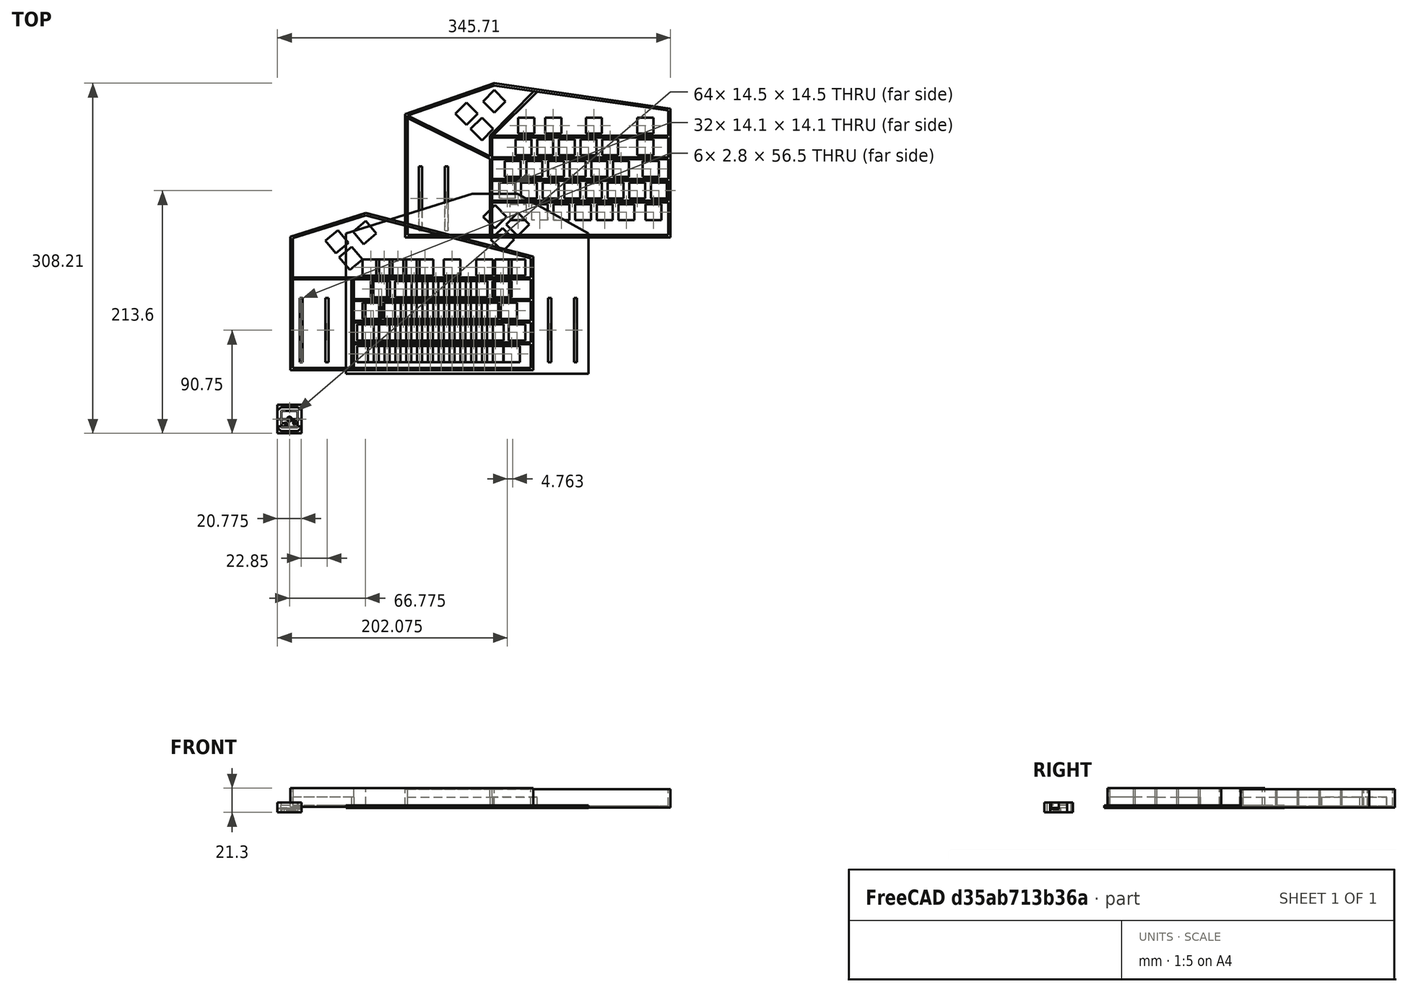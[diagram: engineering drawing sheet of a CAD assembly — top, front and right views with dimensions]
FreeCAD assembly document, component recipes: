
FREECAD ASSEMBLY — COMPONENT RECIPES ("keyboard.FCStd.bak")

This assembly document has 5 components, labeled P0..P4 below (a component is one placed body or linked part). 4 of them carry a construction recipe — the FreeCAD feature program that regenerates the part from scratch, quoted from this document or its linked companion documents; the rest are supplied as boundary geometry only. No exploded tour is included for this assembly.
COMPONENT P0 — recipe-attached ("Body", modeled in this document).
Construction recipe (the document's own serialized feature program — sketch geometry with constraints, then the solid features built on it; lengths are millimeters unless a unit is written):

FEATURE [Sketcher::SketchObject] Sketch
  FullyConstrained = true
  MapMode = 5
  Support = -> [XY_Plane001]
  sketch-geometry (8):
    g0: LineSegment StartX=-7.5 StartY=7.5 StartZ=0 EndX=7.5 EndY=7.5 EndZ=0
    g1: LineSegment StartX=7.5 StartY=7.5 StartZ=0 EndX=7.5 EndY=-7.5 EndZ=0
    g2: LineSegment StartX=7.5 StartY=-7.5 StartZ=0 EndX=-7.5 EndY=-7.5 EndZ=0
    g3: LineSegment StartX=-7.5 StartY=-7.5 StartZ=0 EndX=-7.5 EndY=7.5 EndZ=0
    g4: LineSegment StartX=-10.5 StartY=10.5 StartZ=0 EndX=10.5 EndY=10.5 EndZ=0
    g5: LineSegment StartX=10.5 StartY=10.5 StartZ=0 EndX=10.5 EndY=-10.5 EndZ=0
    g6: LineSegment StartX=10.5 StartY=-10.5 StartZ=0 EndX=-10.5 EndY=-10.5 EndZ=0
    g7: LineSegment StartX=-10.5 StartY=-10.5 StartZ=0 EndX=-10.5 EndY=10.5 EndZ=0
  constraints (20):
    c: Coincident(g0,g1)
    c: Coincident(g1,g2)
    c: Coincident(g2,g3)
    c: Coincident(g3,g0)
    c: Horizontal(g2)
    c: Vertical(g1)
    c: Symmetric(g0,g0,g-2)
    c: Symmetric(g0,g2,g-1)
    c: Equal(g0,g3)
    c: DistanceX(g0,g0) = 15
    c: Coincident(g4,g5)
    c: Coincident(g5,g6)
    c: Coincident(g6,g7)
    c: Coincident(g7,g4)
    c: Horizontal(g6)
    c: Vertical(g5)
    c: Symmetric(g4,g4,g-2)
    c: Symmetric(g4,g6,g-1)
    c: Equal(g4,g7)
    c: DistanceX(g4,g0) = 3
FEATURE [PartDesign::Pad] Pad
  Direction = (0,0,1)
  Length = 2.5
  Length2 = 10
  Profile = -> Sketch
  ReferenceAxis = -> Sketch [N_Axis]
  Type = 0
FEATURE [Sketcher::SketchObject] Sketch001
  ExternalGeometry = -> [Pad]
  FullyConstrained = true
  MapMode = 5
  Placement = pos=(0,0,0) rot=(1,0,0;3.14159rad)
  Support = -> [Pad]
  expr: Constraints[11] = 4.15 / 2
  sketch-geometry (5):
    g0: LineSegment StartX=-10.5 StartY=10.5 StartZ=0 EndX=10.5 EndY=10.5 EndZ=0
    g1: LineSegment StartX=10.5 StartY=10.5 StartZ=0 EndX=10.5 EndY=-10.5 EndZ=0
    g2: LineSegment StartX=10.5 StartY=-10.5 StartZ=0 EndX=-10.5 EndY=-10.5 EndZ=0
    g3: LineSegment StartX=-10.5 StartY=-10.5 StartZ=0 EndX=-10.5 EndY=10.5 EndZ=0
    g4: Circle CenterX=0 CenterY=0 CenterZ=0 NormalX=0 NormalY=0 NormalZ=1 AngleXU=0 Radius=2.075
  constraints (12):
    c: Coincident(g0,g1)
    c: Coincident(g1,g2)
    c: Coincident(g2,g3)
    c: Coincident(g3,g0)
    c: Horizontal(g0)
    c: Horizontal(g2)
    c: Vertical(g1)
    c: Vertical(g3)
    c: Coincident(g0,g-3)
    c: Coincident(g1,g-4)
    c: Coincident(g4,g-1)
    c: Radius(g4) = 2.075
FEATURE [PartDesign::Pad] Pad001
  BaseFeature = -> Pad
  Direction = (0,0,-1)
  Length = 4
  Length2 = 10
  Profile = -> Sketch001
  ReferenceAxis = -> Sketch001 [N_Axis]
  Type = 0
FEATURE [Sketcher::SketchObject] Sketch002
  ExternalGeometry = -> [Pad001]
  FullyConstrained = true
  MapMode = 5
  Placement = pos=(0,0,2.5) rot=(0,0,1;0rad)
  Support = -> [Pad001]
  sketch-geometry (8):
    g0: LineSegment StartX=-10.5 StartY=10.5 StartZ=0 EndX=10.5 EndY=10.5 EndZ=0
    g1: LineSegment StartX=10.5 StartY=10.5 StartZ=0 EndX=10.5 EndY=-10.5 EndZ=0
    g2: LineSegment StartX=10.5 StartY=-10.5 StartZ=0 EndX=-10.5 EndY=-10.5 EndZ=0
    g3: LineSegment StartX=-10.5 StartY=-10.5 StartZ=0 EndX=-10.5 EndY=10.5 EndZ=0
    g4: LineSegment StartX=-7.25 StartY=7.25 StartZ=0 EndX=7.25 EndY=7.25 EndZ=0
    g5: LineSegment StartX=7.25 StartY=7.25 StartZ=0 EndX=7.25 EndY=-7.25 EndZ=0
    g6: LineSegment StartX=7.25 StartY=-7.25 StartZ=0 EndX=-7.25 EndY=-7.25 EndZ=0
    g7: LineSegment StartX=-7.25 StartY=-7.25 StartZ=0 EndX=-7.25 EndY=7.25 EndZ=0
  constraints (20):
    c: Coincident(g0,g1)
    c: Coincident(g1,g2)
    c: Coincident(g2,g3)
    c: Coincident(g3,g0)
    c: Horizontal(g0)
    c: Horizontal(g2)
    c: Vertical(g1)
    c: Vertical(g3)
    c: Coincident(g0,g-3)
    c: Coincident(g1,g-4)
    c: Coincident(g4,g5)
    c: Coincident(g5,g6)
    c: Coincident(g6,g7)
    c: Coincident(g7,g4)
    c: Horizontal(g6)
    c: Vertical(g5)
    c: Symmetric(g4,g4,g-2)
    c: Symmetric(g4,g6,g-1)
    c: DistanceX(g4,g4) = 14.5
    c: Equal(g7,g4)
FEATURE [PartDesign::Pad] Pad002
  BaseFeature = -> Pad001
  Direction = (0,0,1)
  Length = 2.3
  Length2 = 10
  Profile = -> Sketch002
  ReferenceAxis = -> Sketch002 [N_Axis]
  Type = 0
FEATURE [PartDesign::Chamfer] Chamfer
  Angle = 45
  Base = -> Pad002 [Edge19,Edge23,Edge11,Edge12]
  BaseFeature = -> Pad002
  ChamferType = 0
  FlipDirection = false
  Size = 3
  Size2 = 1
  SupportTransform = false
  UseAllEdges = false
FEATURE [Sketcher::SketchObject] Sketch003
  FullyConstrained = true
  MapMode = 5
  Placement = pos=(0,0,-4) rot=(1,0,0;3.14159rad)
  Support = -> [Chamfer]
  sketch-geometry (2):
    g0: Circle CenterX=4 CenterY=2.85 CenterZ=0 NormalX=0 NormalY=0 NormalZ=1 AngleXU=0 Radius=0.75
    g1: Circle CenterX=-2.9 CenterY=5 CenterZ=0 NormalX=0 NormalY=0 NormalZ=1 AngleXU=0 Radius=0.75
  constraints (6):
    c: DistanceX(g-1,g0) = 4
    c: DistanceY(g-1,g0) = 2.85
    c: Radius(g0) = 0.75
    c: DistanceX(g1,g-1) = 2.9
    c: DistanceY(g-1,g1) = 5
    c: Equal(g1,g0)
FEATURE [PartDesign::Pocket] Pocket
  BaseFeature = -> Chamfer
  Direction = (0,0,1)
  Length = 5
  Length2 = 5
  Profile = -> Sketch003
  ReferenceAxis = -> Sketch003 [N_Axis]
  Type = 1
FEATURE [PartDesign::Chamfer] Chamfer001
  Angle = 45
  Base = -> Pocket [Edge27,Edge26]
  BaseFeature = -> Pocket
  ChamferType = 1
  FlipDirection = false
  Size = 1.8
  Size2 = 3.999
  SupportTransform = false
  UseAllEdges = false
FEATURE [PartDesign::Body] Body
  Group = -> [Sketch,Pad,Sketch001,Pad001,Sketch002,Pad002,Chamfer,Sketch003,Pocket,Chamfer001]
  Origin = -> Origin001
  Tip = -> Chamfer001
COMPONENT P1 — recipe-attached ("Body001", modeled in this document).
Construction recipe (the document's own serialized feature program — sketch geometry with constraints, then the solid features built on it; lengths are millimeters unless a unit is written):

FEATURE [Sketcher::SketchObject] Sketch004
  FullyConstrained = true
  MapMode = 5
  Support = -> [XY_Plane002]
  sketch-geometry (8):
    g0: LineSegment StartX=-7.5 StartY=7.5 StartZ=0 EndX=7.5 EndY=7.5 EndZ=0
    g1: LineSegment StartX=7.5 StartY=7.5 StartZ=0 EndX=7.5 EndY=-7.5 EndZ=0
    g2: LineSegment StartX=7.5 StartY=-7.5 StartZ=0 EndX=-7.5 EndY=-7.5 EndZ=0
    g3: LineSegment StartX=-7.5 StartY=-7.5 StartZ=0 EndX=-7.5 EndY=7.5 EndZ=0
    g4: LineSegment StartX=-10.5 StartY=10.5 StartZ=0 EndX=10.5 EndY=10.5 EndZ=0
    g5: LineSegment StartX=10.5 StartY=10.5 StartZ=0 EndX=10.5 EndY=-10.5 EndZ=0
    g6: LineSegment StartX=10.5 StartY=-10.5 StartZ=0 EndX=-10.5 EndY=-10.5 EndZ=0
    g7: LineSegment StartX=-10.5 StartY=-10.5 StartZ=0 EndX=-10.5 EndY=10.5 EndZ=0
  constraints (20):
    c: Coincident(g0,g1)
    c: Coincident(g1,g2)
    c: Coincident(g2,g3)
    c: Coincident(g3,g0)
    c: Horizontal(g2)
    c: Vertical(g1)
    c: Symmetric(g0,g0,g-2)
    c: Symmetric(g0,g2,g-1)
    c: Equal(g0,g3)
    c: DistanceX(g0,g0) = 15
    c: Coincident(g4,g5)
    c: Coincident(g5,g6)
    c: Coincident(g6,g7)
    c: Coincident(g7,g4)
    c: Horizontal(g6)
    c: Vertical(g5)
    c: Symmetric(g4,g4,g-2)
    c: Symmetric(g4,g6,g-1)
    c: Equal(g4,g7)
    c: DistanceX(g4,g0) = 3
FEATURE [PartDesign::Pad] Pad003
  Direction = (0,0,1)
  Length = 2.5
  Length2 = 10
  Profile = -> Sketch004
  ReferenceAxis = -> Sketch004 [N_Axis]
  Type = 0
FEATURE [Sketcher::SketchObject] Sketch005
  ExternalGeometry = -> [Pad003]
  FullyConstrained = true
  MapMode = 5
  Placement = pos=(0,0,0) rot=(1,0,0;3.14159rad)
  Support = -> [Pad003]
  expr: Constraints[11] = 4.15 / 2
  sketch-geometry (5):
    g0: LineSegment StartX=-10.5 StartY=10.5 StartZ=0 EndX=10.5 EndY=10.5 EndZ=0
    g1: LineSegment StartX=10.5 StartY=10.5 StartZ=0 EndX=10.5 EndY=-10.5 EndZ=0
    g2: LineSegment StartX=10.5 StartY=-10.5 StartZ=0 EndX=-10.5 EndY=-10.5 EndZ=0
    g3: LineSegment StartX=-10.5 StartY=-10.5 StartZ=0 EndX=-10.5 EndY=10.5 EndZ=0
    g4: Circle CenterX=0 CenterY=0 CenterZ=0 NormalX=0 NormalY=0 NormalZ=1 AngleXU=0 Radius=2.075
  constraints (12):
    c: Coincident(g0,g1)
    c: Coincident(g1,g2)
    c: Coincident(g2,g3)
    c: Coincident(g3,g0)
    c: Horizontal(g0)
    c: Horizontal(g2)
    c: Vertical(g1)
    c: Vertical(g3)
    c: Coincident(g0,g-3)
    c: Coincident(g1,g-4)
    c: Coincident(g4,g-1)
    c: Radius(g4) = 2.075
FEATURE [PartDesign::Pad] Pad004
  BaseFeature = -> Pad003
  Direction = (0,0,-1)
  Length = 4
  Length2 = 10
  Profile = -> Sketch005
  ReferenceAxis = -> Sketch005 [N_Axis]
  Type = 0
FEATURE [Sketcher::SketchObject] Sketch006
  ExternalGeometry = -> [Pad004]
  FullyConstrained = true
  MapMode = 5
  Placement = pos=(0,0,2.5) rot=(0,0,1;0rad)
  Support = -> [Pad004]
  sketch-geometry (8):
    g0: LineSegment StartX=-10.5 StartY=10.5 StartZ=0 EndX=10.5 EndY=10.5 EndZ=0
    g1: LineSegment StartX=10.5 StartY=10.5 StartZ=0 EndX=10.5 EndY=-10.5 EndZ=0
    g2: LineSegment StartX=10.5 StartY=-10.5 StartZ=0 EndX=-10.5 EndY=-10.5 EndZ=0
    g3: LineSegment StartX=-10.5 StartY=-10.5 StartZ=0 EndX=-10.5 EndY=10.5 EndZ=0
    g4: LineSegment StartX=-7.25 StartY=7.25 StartZ=0 EndX=7.25 EndY=7.25 EndZ=0
    g5: LineSegment StartX=7.25 StartY=7.25 StartZ=0 EndX=7.25 EndY=-7.25 EndZ=0
    g6: LineSegment StartX=7.25 StartY=-7.25 StartZ=0 EndX=-7.25 EndY=-7.25 EndZ=0
    g7: LineSegment StartX=-7.25 StartY=-7.25 StartZ=0 EndX=-7.25 EndY=7.25 EndZ=0
  constraints (20):
    c: Coincident(g0,g1)
    c: Coincident(g1,g2)
    c: Coincident(g2,g3)
    c: Coincident(g3,g0)
    c: Horizontal(g0)
    c: Horizontal(g2)
    c: Vertical(g1)
    c: Vertical(g3)
    c: Coincident(g0,g-3)
    c: Coincident(g1,g-4)
    c: Coincident(g4,g5)
    c: Coincident(g5,g6)
    c: Coincident(g6,g7)
    c: Coincident(g7,g4)
    c: Horizontal(g6)
    c: Vertical(g5)
    c: Symmetric(g4,g4,g-2)
    c: Symmetric(g4,g6,g-1)
    c: DistanceX(g4,g4) = 14.5
    c: Equal(g7,g4)
FEATURE [PartDesign::Pad] Pad005
  BaseFeature = -> Pad004
  Direction = (0,0,1)
  Length = 2.3
  Length2 = 10
  Profile = -> Sketch006
  ReferenceAxis = -> Sketch006 [N_Axis]
  Type = 0
FEATURE [Sketcher::SketchObject] Sketch007
  ExternalGeometry = -> [Pad005]
  FullyConstrained = true
  MapMode = 5
  Placement = pos=(0,0,-4) rot=(1,0,0;3.14159rad)
  Support = -> [Pad005]
  sketch-geometry (22):
    g0: LineSegment StartX=-7.5 StartY=6.5 StartZ=0 EndX=-2 EndY=6.5 EndZ=0
    g1: LineSegment StartX=-2 StartY=6.5 StartZ=0 EndX=-2 EndY=3.5 EndZ=0
    g2: LineSegment StartX=-2 StartY=3.5 StartZ=0 EndX=-7.5 EndY=3.5 EndZ=0
    g3: LineSegment StartX=-7.5 StartY=3.5 StartZ=0 EndX=-7.5 EndY=6.5 EndZ=0
    g4: LineSegment StartX=3 StartY=4.35 StartZ=0 EndX=7.5 EndY=4.35 EndZ=0
    g5: LineSegment StartX=7.5 StartY=4.35 StartZ=0 EndX=7.5 EndY=1.35 EndZ=0
    g6: LineSegment StartX=7.5 StartY=1.35 StartZ=0 EndX=3 EndY=1.35 EndZ=0
    g7: LineSegment StartX=3 StartY=1.35 StartZ=0 EndX=3 EndY=4.35 EndZ=0
    g8: Circle CenterX=-2.9 CenterY=5 CenterZ=0 NormalX=0 NormalY=0 NormalZ=1 AngleXU=0 Radius=0.75
    g9: Circle CenterX=4 CenterY=2.85 CenterZ=0 NormalX=0 NormalY=0 NormalZ=1 AngleXU=0 Radius=0.75
    g10: LineSegment StartX=-2.9 StartY=5 StartZ=0 EndX=-7.5 EndY=5 EndZ=0
    g11: LineSegment StartX=-7.5 StartY=5 StartZ=0 EndX=-7.5 EndY=6.5 EndZ=0
    g12: LineSegment StartX=-7.5 StartY=5 StartZ=0 EndX=-7.5 EndY=3.5 EndZ=0
    g13: LineSegment StartX=4 StartY=2.85 StartZ=0 EndX=7.5 EndY=2.85 EndZ=0
    g14: LineSegment StartX=7.5 StartY=2.85 StartZ=0 EndX=7.5 EndY=1.35 EndZ=0
    g15: LineSegment StartX=7.5 StartY=2.85 StartZ=0 EndX=7.5 EndY=4.35 EndZ=0
    g16: LineSegment StartX=3 StartY=4.35 StartZ=0 EndX=3.8 EndY=3.57284 EndZ=0
    g17: LineSegment StartX=3 StartY=1.35 StartZ=0 EndX=3.8 EndY=2.12716 EndZ=0
    g18: ArcOfCircle CenterX=4 CenterY=2.85 CenterZ=0 NormalX=0 NormalY=0 NormalZ=1 AngleXU=0 Radius=0.75 StartAngle=1.84073 EndAngle=4.44246
    g19: LineSegment StartX=-2 StartY=6.5 StartZ=0 EndX=-2.7 EndY=5.72284 EndZ=0
    g20: LineSegment StartX=-2 StartY=3.5 StartZ=0 EndX=-2.7 EndY=4.27716 EndZ=0
    g21: ArcOfCircle CenterX=-2.9 CenterY=5 CenterZ=0 NormalX=0 NormalY=0 NormalZ=1 AngleXU=0 Radius=0.75 StartAngle=4.98232 EndAngle=7.58405
  constraints (60):
    c: Coincident(g0,g1)
    c: Coincident(g1,g2)
    c: Coincident(g2,g3)
    c: Coincident(g3,g0)
    c: Horizontal(g0)
    c: Horizontal(g2)
    c: Vertical(g1)
    c: Vertical(g3)
    c: Coincident(g4,g5)
    c: Coincident(g5,g6)
    c: Coincident(g6,g7)
    c: Coincident(g7,g4)
    c: Horizontal(g4)
    c: Horizontal(g6)
    c: Vertical(g5)
    c: Vertical(g7)
    c: PointOnObject(g4,g-4)
    c: PointOnObject(g0,g-3)
    c: DistanceY(g-1,g9) = 2.85
    c: DistanceX(g-1,g9) = 4
    c: Radius(g9) = 0.75
    c: DistanceY(g-1,g8) = 5
    c: DistanceX(g8,g-1) = 2.9
    c: Radius(g8) = 0.75
    c: Coincident(g10,g8)
    c: PointOnObject(g10,g-3)
    c: Coincident(g11,g10)
    c: Equal(g12,g11)
    c: Coincident(g12,g10)
    c: Horizontal(g10)
    c: Coincident(g12,g2)
    c: Coincident(g11,g0)
    c: Coincident(g13,g9)
    c: PointOnObject(g13,g-4)
    c: Coincident(g14,g13)
    c: Coincident(g15,g13)
    c: Equal(g15,g14)
    c: Horizontal(g13)
    c: Coincident(g15,g4)
    c: Coincident(g14,g5)
    c: DistanceX(g6,g5) = 4.5
    c: DistanceX(g2,g2) = 5.5
    c: DistanceY(g1,g1) = 3
    c: Coincident(g16,g4)
    c: Coincident(g17,g6)
    c: Coincident(g18,g9)
    c: Coincident(g18,g16)
    c: Coincident(g18,g17)
    c: Equal(g18,g9)
    c: DistanceX(g17,g18) = 0.2
    c: Equal(g16,g17)
    c: Coincident(g19,g0)
    c: PointOnObject(g19,g8)
    c: Coincident(g20,g2)
    c: Coincident(g21,g8)
    c: Coincident(g21,g19)
    c: Coincident(g21,g20)
    c: Equal(g19,g20)
    c: DistanceX(g21,g20) = 0.2
    c: Equal(g1,g7)
FEATURE [PartDesign::Pocket] Pocket001
  BaseFeature = -> Pad005
  Direction = (0,0,1)
  Length = 0
  Length2 = 5
  Profile = -> Sketch007
  ReferenceAxis = -> Sketch007 [N_Axis]
  Type = 3
  UpToFace = -> Pad005 [Face20]
FEATURE [PartDesign::Fillet] Fillet
  Base = -> Pocket001 [Edge65,Edge68,Edge49,Edge53]
  BaseFeature = -> Pocket001
  Radius = 1
  SupportTransform = false
  UseAllEdges = false
FEATURE [Sketcher::SketchObject] Sketch008
  ExternalGeometry = -> [Fillet]
  FullyConstrained = true
  MapMode = 5
  Placement = pos=(0,0,4.8) rot=(0,0,1;0rad)
  Support = -> [Fillet]
  sketch-geometry (4):
    g0: LineSegment StartX=-10.5 StartY=0 StartZ=0 EndX=10.5 EndY=0 EndZ=0
    g1: LineSegment StartX=10.5 StartY=0 StartZ=0 EndX=10.5 EndY=-6.5 EndZ=0
    g2: LineSegment StartX=10.5 StartY=-6.5 StartZ=0 EndX=-10.5 EndY=-6.5 EndZ=0
    g3: LineSegment StartX=-10.5 StartY=-6.5 StartZ=0 EndX=-10.5 EndY=0 EndZ=0
  constraints (11):
    c: Coincident(g0,g1)
    c: Coincident(g1,g2)
    c: Coincident(g2,g3)
    c: Coincident(g3,g0)
    c: Horizontal(g2)
    c: Vertical(g1)
    c: Vertical(g3)
    c: PointOnObject(g0,g-1)
    c: PointOnObject(g2,g-3)
    c: Symmetric(g0,g0,g-2)
    c: PointOnObject(g2,g-4)
FEATURE [PartDesign::Pocket] Pocket002
  BaseFeature = -> Fillet
  Direction = (0,0,-1)
  Length = 0
  Length2 = 5
  Profile = -> Sketch008
  ReferenceAxis = -> Sketch008 [N_Axis]
  Type = 3
  UpToFace = -> Fillet [Face23]
FEATURE [PartDesign::Pad] Pad006
  BaseFeature = -> Pocket002
  Direction = (0,-1,0)
  Length = 2
  Length2 = 10
  Profile = -> Pocket002 [Face10,Face26,Face39]
  Type = 0
FEATURE [PartDesign::Pad] Pad007
  BaseFeature = -> Pad006
  Direction = (0,1,0)
  Length = 2
  Length2 = 10
  Profile = -> Pad006 [Face13,Face34,Face50]
  Type = 0
FEATURE [PartDesign::CoordinateSystem] Local_CS
  AttacherType = Attacher::AttachEngine3D
  MapMode = 45
  Placement = pos=(3.31163,-2.85,0) rot=(0,0.707107,0.707107;3.14159rad)
  Support = -> [Pad007]
FEATURE [PartDesign::CoordinateSystem] Local_CS001
  AttacherType = Attacher::AttachEngine3D
  MapMode = 45
  Placement = pos=(-2.22398,-5,0) rot=(0,0.707107,0.707107;3.14159rad)
  Support = -> [Pad007]
FEATURE [PartDesign::Body] Body001
  Group = -> [Sketch004,Pad003,Sketch005,Pad004,Sketch006,Pad005,Sketch007,Pocket001,Fillet,Sketch008,Pocket002,Pad006,Pad007,Local_CS,Local_CS001]
  Origin = -> Origin002
  Tip = -> Pad007
COMPONENT P2 — geometry summary ("Model"; no construction recipe available for this part):
  bounding box: 16.1 x 4.1 x 4.0 mm
  tessellated surface: 228 triangles
  volume: 2451513960528901609903646099353169505613957827253961644439277037358750804026721693641421339358597268239748682215783712032644430022589533140220938276317429760 mm^3 (915252545422869498662315967676567421757163301824653543720582276189938750638123076976993345633309426533124652158865058795889452386300277657998858502413484032% of its bounding box)
  symmetry: 2-fold rotationally symmetric about the z axis
COMPONENT P3 — recipe-attached ("spring", modeled in this document).
Construction recipe (the document's own serialized feature program — sketch geometry with constraints, then the solid features built on it; lengths are millimeters unless a unit is written):

FEATURE [Sketcher::SketchObject] Sketch013
  FullyConstrained = true
  MapMode = 5
  Support = -> [XY_Plane008]
  sketch-geometry (6):
    g0: ArcOfCircle CenterX=-0.866025 CenterY=0 CenterZ=0 NormalX=0 NormalY=0 NormalZ=1 AngleXU=0 Radius=1 StartAngle=5.75959 EndAngle=6.80678
    g1: LineSegment StartX=0 StartY=0.5 StartZ=0 EndX=0 EndY=1 EndZ=0
    g2: LineSegment StartX=0 StartY=1 StartZ=0 EndX=1 EndY=1 EndZ=0
    g3: LineSegment StartX=1 StartY=1 StartZ=0 EndX=1 EndY=-1 EndZ=0
    g4: LineSegment StartX=1 StartY=-1 StartZ=0 EndX=0 EndY=-1 EndZ=0
    g5: LineSegment StartX=0 StartY=-1 StartZ=0 EndX=2e-16 EndY=-0.5 EndZ=0
  constraints (19):
    c: PointOnObject(g0,g-1)
    c: PointOnObject(g0,g-2)
    c: PointOnObject(g0,g-2)
    c: Coincident(g1,g2)
    c: Horizontal(g2)
    c: Coincident(g2,g3)
    c: Coincident(g3,g4)
    c: PointOnObject(g4,g-2)
    c: Horizontal(g4)
    c: Coincident(g4,g5)
    c: Coincident(g5,g0)
    c: PointOnObject(g1,g-2)
    c: Vertical(g3)
    c: DistanceY(g3,g3) = 2
    c: Radius(g0) = 1
    c: Coincident(g1,g0)
    c: Equal(g1,g5)
    c: DistanceY(g0,g0) = 1
    c: DistanceX(g2,g2) = 1
FEATURE [PartDesign::Pad] Pad011
  Direction = (0,0,1)
  Length = 4
  Length2 = 10
  Profile = -> Sketch013
  ReferenceAxis = -> Sketch013 [N_Axis]
  Reversed = true
  Type = 0
FEATURE [Sketcher::SketchObject] Sketch014
  ExternalGeometry = -> [Pad011]
  FullyConstrained = true
  MapMode = 5
  Support = -> [XY_Plane008]
  sketch-geometry (21):
    g0: LineSegment StartX=1 StartY=1 StartZ=0 EndX=1.66667 EndY=-0.8 EndZ=0
    g1: LineSegment StartX=1.66667 StartY=-0.8 StartZ=0 EndX=2.33333 EndY=1 EndZ=0
    g2: LineSegment StartX=2.33333 StartY=1 StartZ=0 EndX=3 EndY=-0.8 EndZ=0
    g3: LineSegment StartX=3 StartY=-0.8 StartZ=0 EndX=3.66667 EndY=1 EndZ=0
    g4: LineSegment StartX=3.66667 StartY=1 StartZ=0 EndX=4.33333 EndY=-0.8 EndZ=0
    g5: LineSegment StartX=4.33333 StartY=-0.8 StartZ=0 EndX=5 EndY=1 EndZ=0
    g6: LineSegment StartX=1 StartY=1 StartZ=0 EndX=5 EndY=1 EndZ=0
    g7: LineSegment StartX=1 StartY=-1 StartZ=0 EndX=4.33333 EndY=-1 EndZ=0
    g8: LineSegment StartX=1 StartY=0.8 StartZ=0 EndX=1.66667 EndY=-1 EndZ=0
    g9: LineSegment StartX=1.66667 StartY=-1 StartZ=0 EndX=2.33333 EndY=0.8 EndZ=0
    g10: LineSegment StartX=2.33333 StartY=0.8 StartZ=0 EndX=3 EndY=-1 EndZ=0
    g11: LineSegment StartX=3 StartY=-1 StartZ=0 EndX=3.66667 EndY=0.8 EndZ=0
    g12: LineSegment StartX=3.66667 StartY=0.8 StartZ=0 EndX=4.33333 EndY=-1 EndZ=0
    g13: LineSegment StartX=4.33333 StartY=-1 StartZ=0 EndX=5 EndY=0.8 EndZ=0
    g14: LineSegment StartX=1.66667 StartY=-0.8 StartZ=0 EndX=1.66667 EndY=-1 EndZ=0
    g15: LineSegment StartX=3 StartY=-0.8 StartZ=0 EndX=3 EndY=-1 EndZ=0
    g16: LineSegment StartX=2.33333 StartY=0.8 StartZ=0 EndX=2.33333 EndY=1 EndZ=0
    g17: LineSegment StartX=3.66667 StartY=0.8 StartZ=0 EndX=3.66667 EndY=1 EndZ=0
    g18: LineSegment StartX=5 StartY=0.8 StartZ=0 EndX=5 EndY=1 EndZ=0
    g19: LineSegment StartX=4.33333 StartY=-0.8 StartZ=0 EndX=4.33333 EndY=-1 EndZ=0
    g20: LineSegment StartX=1 StartY=0.8 StartZ=0 EndX=1 EndY=1 EndZ=0
  constraints (55):
    c: Coincident(g-3,g0)
    c: Coincident(g0,g1)
    c: Coincident(g1,g2)
    c: Coincident(g2,g3)
    c: Coincident(g3,g4)
    c: Coincident(g6,g0)
    c: Coincident(g6,g5)
    c: Coincident(g7,g-3)
    c: Horizontal(g7)
    c: Horizontal(g6)
    c: PointOnObject(g3,g6)
    c: PointOnObject(g1,g6)
    c: Coincident(g5,g4)
    c: PointOnObject(g8,g-3)
    c: PointOnObject(g8,g7)
    c: Coincident(g8,g9)
    c: Coincident(g9,g10)
    c: PointOnObject(g10,g7)
    c: Coincident(g10,g11)
    c: Coincident(g11,g12)
    c: Coincident(g12,g7)
    c: Coincident(g12,g13)
    c: Coincident(g14,g0)
    c: Coincident(g14,g8)
    c: Coincident(g15,g2)
    c: Coincident(g15,g10)
    c: Coincident(g16,g9)
    c: Coincident(g16,g1)
    c: Coincident(g17,g11)
    c: Coincident(g17,g3)
    c: Vertical(g17)
    c: Coincident(g18,g13)
    c: Coincident(g18,g5)
    c: Coincident(g19,g4)
    c: Coincident(g19,g12)
    c: Equal(g14,g16)
    c: Equal(g16,g15)
    c: Equal(g15,g17)
    c: Equal(g17,g19)
    c: Equal(g19,g18)
    c: Vertical(g14)
    c: Vertical(g16)
    c: Vertical(g15)
    c: Vertical(g18)
    c: Vertical(g19)
    c: Equal(g0,g1)
    c: Equal(g2,g3)
    c: Equal(g3,g4)
    c: Equal(g4,g5)
    c: Equal(g5,g8)
    c: Equal(g8,g9)
    c: Coincident(g20,g8)
    c: Coincident(g20,g0)
    c: DistanceY(g18,g18) = 0.2
    c: DistanceX(g6,g6) = 4
FEATURE [PartDesign::Pad] Pad012
  BaseFeature = -> Pad011
  Direction = (0,0,1)
  Length = 4
  Length2 = 10
  Profile = -> Sketch014
  ReferenceAxis = -> Sketch014 [N_Axis]
  Reversed = true
  Type = 0
FEATURE [PartDesign::Pocket] Pocket006
  BaseFeature = -> Pad012
  Direction = (0,0,-1)
  Length = 1
  Length2 = 5
  Profile = -> Pad012 [Face8]
  Type = 0
FEATURE [Sketcher::SketchObject] Sketch020
  FullyConstrained = true
  MapMode = 5
  Placement = pos=(1,0,0) rot=(0.57735,0.57735,0.57735;2.0944rad)
  Support = -> [Pocket006]
  sketch-geometry (1):
    g0: Circle CenterX=0 CenterY=-0.3 CenterZ=0 NormalX=0 NormalY=0 NormalZ=1 AngleXU=0 Radius=0.65
  constraints (3):
    c: PointOnObject(g0,g-2)
    c: Radius(g0) = 0.65
    c: DistanceY(g0,g-1) = 0.3
FEATURE [PartDesign::Pocket] Pocket007
  BaseFeature = -> Pocket006
  Direction = (-1,0,0)
  Length = 5
  Length2 = 5
  Profile = -> Sketch020
  ReferenceAxis = -> Sketch020 [N_Axis]
  Type = 1
FEATURE [PartDesign::Body] Body_2
  Group = -> [Sketch013,Pad011,Sketch014,Pad012,Pocket006,Sketch020,Pocket007]
  Origin = -> Origin008
  Tip = -> Pocket007
COMPONENT P4 — recipe-attached ("switch_plate", modeled in this document).
Construction recipe (the document's own serialized feature program — sketch geometry with constraints, then the solid features built on it; lengths are millimeters unless a unit is written):

FEATURE [PartDesign::CoordinateSystem] LCS_0004
  AttacherType = Attacher::AttachEngine3D
  MapMode = 2
  Support = -> [X_Axis012]
FEATURE [PartDesign::FeatureBase] BaseFeature
  BaseFeature = -> baseplate_left001001_solid
FEATURE [Sketcher::SketchObject] Sketch021
  ExternalGeometry = -> [BaseFeature]
  FullyConstrained = true
  MapMode = 5
  Placement = pos=(0,0,0) rot=(0,1,0;3.14159rad)
  Support = -> [XY_Plane012]
  sketch-geometry (16):
    g0: LineSegment StartX=-211.098 StartY=171.423 StartZ=0 EndX=-187.375 EndY=147.7 EndZ=0
    g1: LineSegment StartX=-211.098 StartY=171.423 StartZ=0 EndX=-200.845 EndY=181.676 EndZ=0
    g2: LineSegment StartX=-200.845 StartY=181.676 StartZ=0 EndX=-190.592 EndY=171.423 EndZ=0
    g3: LineSegment StartX=-190.592 StartY=171.423 StartZ=0 EndX=-200.845 EndY=161.17 EndZ=0
    g4: LineSegment StartX=-200.845 StartY=161.17 StartZ=0 EndX=-211.098 EndY=171.423 EndZ=0
    g5: LineSegment StartX=-187.375 StartY=147.7 StartZ=0 EndX=-177.122 EndY=157.953 EndZ=0
    g6: LineSegment StartX=-177.122 StartY=157.953 StartZ=0 EndX=-187.375 EndY=168.206 EndZ=0
    g7: LineSegment StartX=-187.375 StartY=168.206 StartZ=0 EndX=-197.628 EndY=157.953 EndZ=0
    g8: LineSegment StartX=-197.628 StartY=157.953 StartZ=0 EndX=-187.375 EndY=147.7 EndZ=0
    g9: LineSegment StartX=-180.64 StartY=167.906 StartZ=0 EndX=-170.387 EndY=178.159 EndZ=0
    g10: LineSegment StartX=-170.387 StartY=178.159 StartZ=0 EndX=-180.64 EndY=188.412 EndZ=0
    g11: LineSegment StartX=-180.64 StartY=188.412 StartZ=0 EndX=-190.893 EndY=178.159 EndZ=0
    g12: LineSegment StartX=-190.893 StartY=178.159 StartZ=0 EndX=-180.64 EndY=167.906 EndZ=0
    g13: LineSegment StartX=-190.592 StartY=171.423 StartZ=0 EndX=-187.375 EndY=174.641 EndZ=0
    g14: LineSegment StartX=-200.845 StartY=181.676 StartZ=0 EndX=-190.893 EndY=178.159 EndZ=0
    g15: LineSegment StartX=-180.64 StartY=167.906 StartZ=0 EndX=-177.122 EndY=157.953 EndZ=0
  constraints (45):
    c: Coincident(g1,g2)
    c: Coincident(g2,g3)
    c: Coincident(g3,g4)
    c: Coincident(g4,g1)
    c: PointOnObject(g3,g0)
    c: Equal(g4,g3)
    c: Equal(g3,g1)
    c: Equal(g1,g2)
    c: Perpendicular(g4,g1)
    c: Distance(g1) = 14.5
    c: Coincident(g0,g1)
    c: Coincident(g0,g5)
    c: Coincident(g5,g6)
    c: Coincident(g6,g7)
    c: PointOnObject(g7,g0)
    c: Coincident(g7,g8)
    c: Coincident(g8,g5)
    c: Equal(g7,g8)
    c: Equal(g8,g6)
    c: Equal(g6,g5)
    c: Equal(g5,g4)
    c: Perpendicular(g8,g7)
    c: Distance(g1,g7) = 19.05
    c: Coincident(g9,g10)
    c: Coincident(g10,g11)
    c: Coincident(g11,g12)
    c: Coincident(g12,g9)
    c: Equal(g11,g12)
    c: Equal(g12,g10)
    c: Equal(g10,g9)
    c: Perpendicular(g12,g11)
    c: Parallel(g2,g12)
    c: Coincident(g13,g2)
    c: PointOnObject(g13,g12)
    c: Perpendicular(g12,g13)
    c: Distance(g13,g3) = 19.05
    c: Coincident(g14,g1)
    c: Coincident(g14,g11)
    c: Coincident(g15,g9)
    c: Coincident(g15,g5)
    c: Equal(g15,g14)
    c: Equal(g6,g10)
    c: Angle(g8,g-1) = 0.785398
    c: DistanceX(g-3,g5) = 20
    c: DistanceY(g-3,g5) = 7
FEATURE [PartDesign::Pocket] Pocket012
  BaseFeature = -> BaseFeature
  Direction = (0,0,1)
  Length = 5
  Length2 = 5
  Profile = -> Sketch021
  ReferenceAxis = -> Sketch021 [N_Axis]
  Type = 0
FEATURE [Sketcher::SketchObject] Sketch022
  ExternalGeometry = -> [Pocket012]
  FullyConstrained = false
  MapMode = 5
  Placement = pos=(0,0,2.3) rot=(0,0,1;0rad)
  Support = -> [Pocket012]
  sketch-geometry (22):
    g0: LineSegment StartX=160.64 StartY=198.412 StartZ=0 EndX=200.64 EndY=198.412 EndZ=0
    g1: LineSegment StartX=49.525 StartY=40 StartZ=0 EndX=263.025 EndY=40 EndZ=0
    g2: LineSegment StartX=227.375 StartY=106.5 StartZ=0 EndX=230.175 EndY=106.5 EndZ=0
    g3: LineSegment StartX=230.175 StartY=106.5 StartZ=0 EndX=230.175 EndY=50 EndZ=0
    g4: LineSegment StartX=230.175 StartY=50 StartZ=0 EndX=227.375 EndY=50 EndZ=0
    g5: LineSegment StartX=227.375 StartY=50 StartZ=0 EndX=227.375 EndY=106.5 EndZ=0
    g6: LineSegment StartX=253.025 StartY=106.5 StartZ=0 EndX=250.225 EndY=106.5 EndZ=0
    g7: LineSegment StartX=250.225 StartY=106.5 StartZ=0 EndX=250.225 EndY=50 EndZ=0
    g8: LineSegment StartX=250.225 StartY=50 StartZ=0 EndX=253.025 EndY=50 EndZ=0
    g9: LineSegment StartX=253.025 StartY=50 StartZ=0 EndX=253.025 EndY=106.5 EndZ=0
    g10: LineSegment StartX=227.375 StartY=106.5 StartZ=0 EndX=228.775 EndY=106.5 EndZ=0
    g11: LineSegment StartX=228.775 StartY=106.5 StartZ=0 EndX=230.175 EndY=106.5 EndZ=0
    g12: LineSegment StartX=253.025 StartY=106.5 StartZ=0 EndX=251.625 EndY=106.5 EndZ=0
    g13: LineSegment StartX=251.625 StartY=106.5 StartZ=0 EndX=250.225 EndY=106.5 EndZ=0
    g14: LineSegment StartX=200.64 StartY=198.412 StartZ=0 EndX=263.025 EndY=163.412 EndZ=0
    g15: LineSegment StartX=263.025 StartY=163.412 StartZ=0 EndX=263.025 EndY=40 EndZ=0
    g16: LineSegment StartX=49.525 StartY=40 StartZ=0 EndX=49.525 EndY=163.412 EndZ=0
    g17: LineSegment StartX=49.525 StartY=163.412 StartZ=0 EndX=160.64 EndY=198.412 EndZ=0
    g18: LineSegment StartX=0 StartY=0 StartZ=0 EndX=511.801 EndY=0 EndZ=0
    g19: LineSegment StartX=511.801 StartY=0 StartZ=0 EndX=511.801 EndY=507.959 EndZ=0
    g20: LineSegment StartX=511.801 StartY=507.959 StartZ=0 EndX=0 EndY=507.959 EndZ=0
    g21: LineSegment StartX=0 StartY=507.959 StartZ=0 EndX=0 EndY=0 EndZ=0
  constraints (61):
    c: Coincident(g0,g14)
    c: Coincident(g17,g0)
    c: Coincident(g1,g15)
    c: Coincident(g2,g3)
    c: Coincident(g3,g4)
    c: Coincident(g4,g5)
    c: Coincident(g5,g2)
    c: Horizontal(g2)
    c: Horizontal(g4)
    c: Vertical(g3)
    c: Vertical(g5)
    c: Coincident(g6,g7)
    c: Coincident(g7,g8)
    c: Coincident(g8,g9)
    c: Coincident(g9,g6)
    c: Horizontal(g6)
    c: Horizontal(g8)
    c: Vertical(g7)
    c: Vertical(g9)
    c: Coincident(g10,g2)
    c: Coincident(g11,g10)
    c: Coincident(g11,g2)
    c: Equal(g11,g10)
    c: PointOnObject(g10,g2)
    c: Coincident(g6,g12)
    c: Coincident(g12,g13)
    c: Coincident(g13,g6)
    c: Equal(g13,g12)
    c: PointOnObject(g12,g6)
    c: DistanceX(g10,g12) = 22.85
    c: Equal(g2,g6)
    c: DistanceX(g4,g4) = 2.8
    c: DistanceY(g5,g5) = 56.5
    c: PointOnObject(g6,g2)
    c: PointOnObject(g8,g4)
    c: Horizontal(g1)
    c: DistanceX(g-3,g2) = 20
    c: DistanceY(g4,g-4) = 0
    c: DistanceY(g15,g-4) = 10
    c: DistanceX(g16,g-6) = 10
    c: DistanceX(g8,g15) = 10
    c: Coincident(g14,g15)
    c: Vertical(g15)
    c: Horizontal(g0)
    c: DistanceY(g-5,g0) = 10
    c: Coincident(g16,g17)
    c: Vertical(g16)
    c: DistanceY(g16,g-5) = 25
    c: DistanceY(g14,g-5) = 25
    c: DistanceX(g0,g-5) = 20
    c: DistanceX(g-5,g0) = 20
    c: Coincident(g1,g16)
    c: Coincident(g18,g19)
    c: Coincident(g19,g20)
    c: Coincident(g20,g21)
    c: Coincident(g21,g18)
    c: Horizontal(g18)
    c: Horizontal(g20)
    c: Vertical(g19)
    c: Vertical(g21)
    c: Coincident(g18,g-1)
FEATURE [PartDesign::Pocket] Pocket013
  BaseFeature = -> Pocket012
  Direction = (0,0,-1)
  Length = 5
  Length2 = 5
  Profile = -> Sketch022
  ReferenceAxis = -> Sketch022 [N_Axis]
  Type = 0
FEATURE [PartDesign::CoordinateSystem] LCS_0005
  AttacherType = Attacher::AttachEngine3D
  MapMode = 2
  Support = -> [X_Axis]
FEATURE [PartDesign::FeatureBase] BaseFeature001
  BaseFeature = -> baseplate_right001001_solid
FEATURE [Sketcher::SketchObject] Sketch024
  ExternalGeometry = -> [BaseFeature001]
  FullyConstrained = true
  MapMode = 5
  Placement = pos=(0,0,0) rot=(1,0,0;3.14159rad)
  Support = -> [BaseFeature001]
  expr: Constraints[40] = 1.25 * 19.05
  sketch-geometry (16):
    g0: LineSegment StartX=42.6282 StartY=-166.401 StartZ=0 EndX=64.1937 EndY=-140.7 EndZ=0
    g1: LineSegment StartX=42.6282 StartY=-166.401 StartZ=0 EndX=31.5206 EndY=-157.08 EndZ=0
    g2: LineSegment StartX=31.5206 StartY=-157.08 StartZ=0 EndX=40.841 EndY=-145.973 EndZ=0
    g3: LineSegment StartX=40.841 StartY=-145.973 StartZ=0 EndX=51.9486 EndY=-155.293 EndZ=0
    g4: LineSegment StartX=51.9486 StartY=-155.293 StartZ=0 EndX=42.6282 EndY=-166.401 EndZ=0
    g5: LineSegment StartX=54.8733 StartY=-151.808 StartZ=0 EndX=43.7657 EndY=-142.487 EndZ=0
    g6: LineSegment StartX=43.7657 StartY=-142.487 StartZ=0 EndX=53.0861 EndY=-131.38 EndZ=0
    g7: LineSegment StartX=53.0861 StartY=-131.38 StartZ=0 EndX=64.1937 EndY=-140.7 EndZ=0
    g8: LineSegment StartX=64.1937 StartY=-140.7 StartZ=0 EndX=54.8733 EndY=-151.808 EndZ=0
    g9: LineSegment StartX=42.6282 StartY=-166.401 StartZ=0 EndX=53.411 EndY=-153.55 EndZ=0
    g10: LineSegment StartX=53.411 StartY=-153.55 StartZ=0 EndX=64.1937 EndY=-140.7 EndZ=0
    g11: LineSegment StartX=53.411 StartY=-153.55 StartZ=0 EndX=71.6524 EndY=-168.857 EndZ=0
    g12: LineSegment StartX=65.205 StartY=-153.983 StartZ=0 EndX=76.3126 EndY=-163.303 EndZ=0
    g13: LineSegment StartX=76.3126 StartY=-163.303 StartZ=0 EndX=66.9922 EndY=-174.411 EndZ=0
    g14: LineSegment StartX=66.9922 StartY=-174.411 StartZ=0 EndX=55.8846 EndY=-165.09 EndZ=0
    g15: LineSegment StartX=55.8846 StartY=-165.09 StartZ=0 EndX=65.205 EndY=-153.983 EndZ=0
  constraints (44):
    c: Coincident(g0,g1)
    c: Coincident(g1,g2)
    c: Coincident(g2,g3)
    c: PointOnObject(g3,g0)
    c: Coincident(g3,g4)
    c: Coincident(g4,g1)
    c: PointOnObject(g5,g0)
    c: Coincident(g5,g6)
    c: Coincident(g6,g7)
    c: Coincident(g7,g0)
    c: Coincident(g7,g8)
    c: Coincident(g8,g5)
    c: Equal(g1,g2)
    c: Equal(g2,g3)
    c: Equal(g3,g4)
    c: Equal(g4,g5)
    c: Equal(g5,g6)
    c: Equal(g6,g7)
    c: Equal(g7,g8)
    c: Perpendicular(g8,g5)
    c: Perpendicular(g4,g1)
    c: Distance(g1,g5) = 19.05
    c: Distance(g2) = 14.5
    c: Coincident(g9,g1)
    c: Coincident(g10,g9)
    c: Coincident(g10,g7)
    c: Equal(g9,g10)
    c: PointOnObject(g9,g0)
    c: Coincident(g11,g9)
    c: Perpendicular(g0,g11)
    c: Coincident(g12,g13)
    c: Coincident(g13,g14)
    c: Coincident(g14,g15)
    c: Coincident(g15,g12)
    c: Symmetric(g12,g14,g11)
    c: Symmetric(g12,g13,g11)
    c: Equal(g12,g15)
    c: Equal(g14,g13)
    c: Equal(g13,g8)
    c: PointOnObject(g11,g13)
    c: Distance(g11,g9) = 23.8125
    c: Angle(g7,g-3) = 0.698132
    c: DistanceX(g7,g-3) = 12
    c: PointOnObject(g7,g-3)
FEATURE [PartDesign::Pocket] Pocket014
  BaseFeature = -> BaseFeature001
  Direction = (0,0,1)
  Length = 5
  Length2 = 5
  Profile = -> Sketch024
  ReferenceAxis = -> Sketch024 [N_Axis]
  Type = 0
FEATURE [Sketcher::SketchObject] Sketch025
  ExternalGeometry = -> [Pocket014]
  FullyConstrained = true
  MapMode = 5
  Placement = pos=(0,0,0) rot=(1,0,0;3.14159rad)
  Support = -> [Pocket014]
  sketch-geometry (24):
    g0: LineSegment StartX=0.875002 StartY=-43 StartZ=0 EndX=214.375 EndY=-43 EndZ=0
    g1: LineSegment StartX=214.375 StartY=-43 StartZ=0 EndX=214.375 EndY=-143.007 EndZ=0
    g2: LineSegment StartX=214.375 StartY=-143.007 StartZ=0 EndX=66.9922 EndY=-181.411 EndZ=0
    g3: LineSegment StartX=66.9922 StartY=-181.411 StartZ=0 EndX=0.875002 EndY=-160.593 EndZ=0
    g4: LineSegment StartX=0.875002 StartY=-160.593 StartZ=0 EndX=0.875002 EndY=-43 EndZ=0
    g5: LineSegment StartX=42.6282 StartY=-166.401 StartZ=0 EndX=40.526 EndY=-173.078 EndZ=0
    g6: LineSegment StartX=66.9922 StartY=-181.411 StartZ=0 EndX=66.9922 EndY=-174.411 EndZ=0
    g7: LineSegment StartX=195.469 StartY=-140.7 StartZ=0 EndX=197.234 EndY=-147.474 EndZ=0
    g8: LineSegment StartX=8.875 StartY=-50 StartZ=0 EndX=11.675 EndY=-50 EndZ=0
    g9: LineSegment StartX=11.675 StartY=-50 StartZ=0 EndX=11.675 EndY=-106.5 EndZ=0
    g10: LineSegment StartX=11.675 StartY=-106.5 StartZ=0 EndX=8.875 EndY=-106.5 EndZ=0
    g11: LineSegment StartX=8.875 StartY=-106.5 StartZ=0 EndX=8.875 EndY=-50 EndZ=0
    g12: LineSegment StartX=31.725 StartY=-50 StartZ=0 EndX=34.525 EndY=-50 EndZ=0
    g13: LineSegment StartX=34.525 StartY=-50 StartZ=0 EndX=34.525 EndY=-106.5 EndZ=0
    g14: LineSegment StartX=34.525 StartY=-106.5 StartZ=0 EndX=31.725 EndY=-106.5 EndZ=0
    g15: LineSegment StartX=31.725 StartY=-106.5 StartZ=0 EndX=31.725 EndY=-50 EndZ=0
    g16: LineSegment StartX=8.875 StartY=-50 StartZ=0 EndX=10.275 EndY=-50 EndZ=0
    g17: LineSegment StartX=10.275 StartY=-50 StartZ=0 EndX=11.675 EndY=-50 EndZ=0
    g18: LineSegment StartX=31.725 StartY=-50 StartZ=0 EndX=33.125 EndY=-50 EndZ=0
    g19: LineSegment StartX=33.125 StartY=-50 StartZ=0 EndX=34.525 EndY=-50 EndZ=0
    g20: LineSegment StartX=0 StartY=0 StartZ=0 EndX=798.95 EndY=0 EndZ=0
    g21: LineSegment StartX=798.95 StartY=0 StartZ=0 EndX=798.95 EndY=-762.419 EndZ=0
    g22: LineSegment StartX=798.95 StartY=-762.419 StartZ=0 EndX=0 EndY=-762.419 EndZ=0
    g23: LineSegment StartX=0 StartY=-762.419 StartZ=0 EndX=0 EndY=0 EndZ=0
  constraints (68):
    c: Horizontal(g0)
    c: Coincident(g0,g1)
    c: Vertical(g1)
    c: Coincident(g1,g2)
    c: Coincident(g2,g3)
    c: Coincident(g3,g4)
    c: Coincident(g4,g0)
    c: Vertical(g4)
    c: DistanceX(g-3,g1) = 7
    c: Coincident(g5,g-4)
    c: PointOnObject(g5,g3)
    c: Perpendicular(g3,g5)
    c: Distance(g5) = 7
    c: Coincident(g6,g2)
    c: Coincident(g6,g-5)
    c: Vertical(g6)
    c: DistanceY(g6,g6) = 7
    c: Coincident(g7,g-6)
    c: PointOnObject(g7,g2)
    c: Perpendicular(g2,g7)
    c: Distance(g7) = 7
    c: DistanceY(g-7,g0) = 7
    c: Coincident(g8,g9)
    c: Coincident(g9,g10)
    c: Coincident(g10,g11)
    c: Coincident(g11,g8)
    c: Horizontal(g8)
    c: Horizontal(g10)
    c: Vertical(g9)
    c: Vertical(g11)
    c: Coincident(g12,g13)
    c: Coincident(g13,g14)
    c: Coincident(g14,g15)
    c: Coincident(g15,g12)
    c: Horizontal(g12)
    c: Horizontal(g14)
    c: Vertical(g13)
    c: Vertical(g15)
    c: Coincident(g16,g8)
    c: Coincident(g17,g16)
    c: Coincident(g17,g8)
    c: Equal(g17,g16)
    c: Horizontal(g16)
    c: Coincident(g12,g18)
    c: Coincident(g18,g19)
    c: Coincident(g19,g12)
    c: Equal(g19,g18)
    c: Horizontal(g19)
    c: PointOnObject(g8,g12)
    c: Equal(g11,g15)
    c: Equal(g10,g14)
    c: DistanceX(g16,g18) = 22.85
    c: DistanceY(g11,g11) = 56.5
    c: DistanceX(g10,g10) = 2.8
    c: DistanceY(g8,g0) = 7
    c: DistanceX(g0,g8) = 8
    c: Coincident(g20,g21)
    c: Coincident(g21,g22)
    c: Coincident(g22,g23)
    c: Coincident(g23,g20)
    c: Horizontal(g20)
    c: Horizontal(g22)
    c: Vertical(g21)
    c: Vertical(g23)
    c: Coincident(g20,g-1)
    c: DistanceX(g21) = 798.95
    c: DistanceY(g21) = -762.419
    c: DistanceX(g12,g-8) = 25
FEATURE [PartDesign::Pocket] Pocket015
  BaseFeature = -> Pocket014
  Direction = (0,0,1)
  Length = 5
  Length2 = 5
  Profile = -> Sketch025
  ReferenceAxis = -> Sketch025 [N_Axis]
  Type = 0
FEATURE [Sketcher::SketchObject] Sketch026
  ExternalGeometry = -> [Pocket015]
  FullyConstrained = true
  MapMode = 5
  Placement = pos=(0,0,2.3) rot=(0,0,1;0rad)
  Support = -> [Pocket015]
  sketch-geometry (10):
    g0: LineSegment StartX=0.875002 StartY=160.593 StartZ=0 EndX=66.9922 EndY=181.411 EndZ=0
    g1: LineSegment StartX=66.9922 StartY=181.411 StartZ=0 EndX=214.375 EndY=143.007 EndZ=0
    g2: LineSegment StartX=214.375 StartY=143.007 StartZ=0 EndX=214.375 EndY=43 EndZ=0
    g3: LineSegment StartX=214.375 StartY=43 StartZ=0 EndX=0.875002 EndY=43 EndZ=0
    g4: LineSegment StartX=0.875002 StartY=43 StartZ=0 EndX=0.875002 EndY=160.593 EndZ=0
    g5: LineSegment StartX=212.375 StartY=141.462 StartZ=0 EndX=212.375 EndY=45 EndZ=0
    g6: LineSegment StartX=212.375 StartY=45 StartZ=0 EndX=2.875 EndY=45 EndZ=0
    g7: LineSegment StartX=2.875 StartY=45 StartZ=0 EndX=2.875 EndY=159.126 EndZ=0
    g8: LineSegment StartX=2.875 StartY=159.126 StartZ=0 EndX=67.0444 EndY=179.33 EndZ=0
    g9: LineSegment StartX=67.0444 StartY=179.33 StartZ=0 EndX=212.375 EndY=141.462 EndZ=0
  constraints (21):
    c: Coincident(g-7,g0)
    c: Coincident(g0,g-4)
    c: Coincident(g0,g1)
    c: Coincident(g1,g-5)
    c: Coincident(g1,g2)
    c: Coincident(g2,g-6)
    c: Coincident(g2,g3)
    c: Coincident(g3,g-7)
    c: Coincident(g3,g4)
    c: Coincident(g4,g0)
    c: Coincident(g5,g6)
    c: Coincident(g5,g9)
    c: Coincident(g6,g7)
    c: Coincident(g7,g8)
    c: Coincident(g8,g9)
    c: Block(g9)
    c: Block(g5)
    c: Parallel(g0,g8)
    c: DistanceX(g3,g6) = 2
    c: Vertical(g7)
    c: Horizontal(g6)
FEATURE [PartDesign::Pad] Pad020
  BaseFeature = -> Pocket015
  Direction = (0,0,1)
  Length = 15
  Length2 = 10
  Profile = -> Sketch026
  ReferenceAxis = -> Sketch026 [N_Axis]
  Type = 0
FEATURE [Sketcher::SketchObject] Sketch027
  ExternalGeometry = -> [Pad020]
  FullyConstrained = true
  MapMode = 5
  Placement = pos=(0,0,2.3) rot=(0,0,1;0rad)
  Support = -> [Pad020]
  sketch-geometry (10):
    g0: LineSegment StartX=88.1 StartY=64.5 StartZ=0 EndX=88.1 EndY=66.775 EndZ=0
    g1: LineSegment StartX=88.1 StartY=66.775 StartZ=0 EndX=88.1 EndY=69.05 EndZ=0
    g2: LineSegment StartX=88.1 StartY=66.775 StartZ=0 EndX=212.375 EndY=66.775 EndZ=0
    g3: LineSegment StartX=56.525 StartY=66 StartZ=0 EndX=56.525 EndY=67.55 EndZ=0
    g4: LineSegment StartX=56.525 StartY=67.55 StartZ=0 EndX=212.375 EndY=67.55 EndZ=0
    g5: LineSegment StartX=212.375 StartY=67.55 StartZ=0 EndX=212.375 EndY=66 EndZ=0
    g6: LineSegment StartX=212.375 StartY=66 StartZ=0 EndX=56.525 EndY=66 EndZ=0
    g7: GeomPoint X=134.45 Y=66.775 Z=0
    g8: LineSegment StartX=97.625 StartY=83.55 StartZ=0 EndX=97.625 EndY=85.825 EndZ=0
    g9: LineSegment StartX=97.625 StartY=85.825 StartZ=0 EndX=97.625 EndY=88.1 EndZ=0
  constraints (29):
    c: Coincident(g-4,g0)
    c: Vertical(g0)
    c: Coincident(g0,g1)
    c: Vertical(g1)
    c: Equal(g1,g0)
    c: Coincident(g2,g0)
    c: PointOnObject(g2,g-3)
    c: Horizontal(g2)
    c: Coincident(g3,g4)
    c: Coincident(g4,g5)
    c: Coincident(g5,g6)
    c: Coincident(g6,g3)
    c: Vertical(g3)
    c: Vertical(g5)
    c: Horizontal(g4)
    c: Horizontal(g6)
    c: Symmetric(g5,g3,g7)
    c: PointOnObject(g7,g2)
    c: PointOnObject(g5,g-3)
    c: PointOnObject(g1,g-5)
    c: DistanceY(g0,g3) = 1.5
    c: DistanceX(g-6,g3) = 22
    c: Coincident(g8,g-7)
    c: Vertical(g8)
    c: Coincident(g9,g8)
    c: PointOnObject(g9,g-8)
    c: Vertical(g9)
    c: Equal(g9,g8)
    c: DistanceY(g0,g8) = 19.05  'wall_row_distance'
FEATURE [PartDesign::Pad] Pad021
  BaseFeature = -> Pad020
  Direction = (0,0,1)
  Length = 20
  Length2 = 10
  Profile = -> Sketch027
  ReferenceAxis = -> Sketch027 [N_Axis]
  Type = 3
  UpToFace = -> Pad020 [Face161]
FEATURE [PartDesign::LinearPattern] LinearPattern
  BaseFeature = -> Pad021
  Direction = -> Sketch027 [V_Axis]
  Length = 57.15
  Mode = 0
  Occurrences = 4
  Offset = 19.05
  Originals = -> [Pad021]
  expr: Length = Sketch027.Constraints.wall_row_distance * (Occurrences - 1)
FEATURE [PartDesign::Pad] Pad022
  BaseFeature = -> LinearPattern
  Direction = (-1,0,0)
  Length = 10
  Length2 = 10
  Profile = -> LinearPattern [Face164]
  Type = 2
FEATURE [PartDesign::Pad] Pad023
  BaseFeature = -> Pad022
  Direction = (-1,0,0)
  Length = 2
  Length2 = 10
  Profile = -> Pad022 [Face170]
  Type = 0
FEATURE [PartDesign::Pad] Pad024
  BaseFeature = -> Pad023
  Direction = (0,-1,0)
  Length = 10
  Length2 = 10
  Profile = -> Pad023 [Face171]
  Type = 2
FEATURE [PartDesign::Pad] Pad025
  BaseFeature = -> Pad024
  Direction = (0,1,0)
  Length = 10
  Length2 = 10
  Profile = -> Pad024 [Face179]
  Type = 2
FEATURE [PartDesign::Pocket] Pocket016
  BaseFeature = -> Pad025
  Direction = (0,0,-1)
  Length = 8
  Length2 = 5
  Profile = -> Pad025 [Face201,Face202,Face199]
  Type = 0
FEATURE [PartDesign::Pocket] Pocket017
  BaseFeature = -> Pocket016
  Direction = (0,0,-1)
  Length = 8
  Length2 = 5
  Profile = -> Pocket016 [Face200]
  Type = 0
FEATURE [PartDesign::Pad] Pad026
  BaseFeature = -> Pocket013
  Direction = (1,0,0)
  Length = 10
  Length2 = 10
  Profile = -> Pocket013 [Face117]
  Type = 2
FEATURE [PartDesign::Body] Body_3  label="plate_left"
  BaseFeature = -> baseplate_left001001_solid
  Group = -> [BaseFeature,LCS_0004,Sketch021,Pocket012,Sketch022,Pocket013,Pad026]
  Origin = -> Origin012
  Tip = -> Pocket013
FEATURE [PartDesign::Pocket] Pocket018
  BaseFeature = -> Pocket017
  Direction = (0,0,1)
  Length = 0.9
  Length2 = 5
  Profile = -> Pocket017 [Face1]
  Type = 0
FEATURE [Sketcher::SketchObject] Sketch028
  FullyConstrained = false
  MapMode = 5
  Placement = pos=(0,0,0.9) rot=(1,0,0;3.14159rad)
  Support = -> [Pocket018]
  sketch-geometry (8):
    g0: LineSegment StartX=186.641 StartY=-48.1554 StartZ=0 EndX=186.641 EndY=-65.87 EndZ=0
    g1: LineSegment StartX=186.641 StartY=-65.87 StartZ=0 EndX=203.656 EndY=-65.87 EndZ=0
    g2: LineSegment StartX=203.656 StartY=-65.87 StartZ=0 EndX=203.656 EndY=-48.1554 EndZ=0
    g3: LineSegment StartX=203.656 StartY=-48.1554 StartZ=0 EndX=186.641 EndY=-48.1554 EndZ=0
    g4: LineSegment StartX=-16.894 StartY=-28.9206 StartZ=0 EndX=-16.894 EndY=-187.952 EndZ=0
    g5: LineSegment StartX=-16.894 StartY=-187.952 StartZ=0 EndX=239.258 EndY=-187.952 EndZ=0
    g6: LineSegment StartX=239.258 StartY=-187.952 StartZ=0 EndX=239.258 EndY=-28.9206 EndZ=0
    g7: LineSegment StartX=239.258 StartY=-28.9206 StartZ=0 EndX=-16.894 EndY=-28.9206 EndZ=0
  constraints (16):
    c: Coincident(g0,g1)
    c: Coincident(g1,g2)
    c: Coincident(g2,g3)
    c: Coincident(g3,g0)
    c: Vertical(g0)
    c: Vertical(g2)
    c: Horizontal(g1)
    c: Horizontal(g3)
    c: Coincident(g4,g5)
    c: Coincident(g5,g6)
    c: Coincident(g6,g7)
    c: Coincident(g7,g4)
    c: Vertical(g4)
    c: Vertical(g6)
    c: Horizontal(g5)
    c: Horizontal(g7)
FEATURE [PartDesign::Pocket] Pocket019
  BaseFeature = -> Pocket018
  Direction = (0,0,1)
  Length = 5
  Length2 = 5
  Profile = -> Sketch028
  ReferenceAxis = -> Sketch028 [N_Axis]
  Type = 1
FEATURE [PartDesign::Pad] Pad027
  BaseFeature = -> Pocket019
  Direction = (-1,0,0)
  Length = 0.4
  Length2 = 10
  Profile = -> Pocket019 [Face8]
  Type = 0
  expr: Length = Spreadsheet.horizontal_pad
FEATURE [PartDesign::Pad] Pad028
  BaseFeature = -> Pad027
  Direction = (0,-1,0)
  Length = 0.4
  Length2 = 10
  Profile = -> Pad027 [Face6]
  Type = 0
  expr: Length = Spreadsheet.horizontal_pad
FEATURE [PartDesign::Body] plate_right
  BaseFeature = -> baseplate_right001001_solid
  Group = -> [BaseFeature001,LCS_0005,Sketch024,Pocket014,Sketch025,Pocket015,Sketch026,Pad020,Sketch027,Pad021,LinearPattern,Pad022,Pad023,Pad024,Pad025,Pocket016,Pocket017,Pocket018,Sketch028,Pocket019,Pad027,Pad028]
  Origin = -> Origin
  Tip = -> Pocket018
FEATURE [PartDesign::FeatureBase] BaseFeature002
  BaseFeature = -> baseplate_right_v004_solid001
FEATURE [Sketcher::SketchObject] Sketch029
  AttachmentOffset = pos=(0,0,10) rot=(0,0,1;0rad)
  ExternalGeometry = -> [BaseFeature002]
  FullyConstrained = true
  MapMode = 5
  Placement = pos=(0,0,10) rot=(0,0,1;0rad)
  Support = -> [XY_Plane013]
  expr: Constraints[24] = Spreadsheet.d_key
  expr: Constraints[9] = Spreadsheet.switch_hole_size
  sketch-geometry (19):
    g0: LineSegment StartX=155.753 StartY=278.77 StartZ=0 EndX=145.783 EndY=268.8 EndZ=0
    g1: LineSegment StartX=145.783 StartY=268.8 StartZ=0 EndX=155.753 EndY=258.83 EndZ=0
    g2: LineSegment StartX=155.753 StartY=258.83 StartZ=0 EndX=165.723 EndY=268.8 EndZ=0
    g3: LineSegment StartX=165.723 StartY=268.8 StartZ=0 EndX=155.753 EndY=278.77 EndZ=0
    g4: GeomPoint X=155.753 Y=268.8 Z=0
    g5: LineSegment StartX=169.224 StartY=265.3 StartZ=0 EndX=159.253 EndY=255.33 EndZ=0
    g6: LineSegment StartX=159.253 StartY=255.33 StartZ=0 EndX=169.224 EndY=245.359 EndZ=0
    g7: LineSegment StartX=169.224 StartY=245.359 StartZ=0 EndX=179.194 EndY=255.33 EndZ=0
    g8: LineSegment StartX=179.194 StartY=255.33 StartZ=0 EndX=169.224 EndY=265.3 EndZ=0
    g9: GeomPoint X=169.224 Y=255.33 Z=0
    g10: LineSegment StartX=155.753 StartY=268.8 StartZ=0 EndX=169.224 EndY=255.33 EndZ=0
    g11: LineSegment StartX=180.166 StartY=289.713 StartZ=0 EndX=170.196 EndY=279.742 EndZ=0
    g12: LineSegment StartX=170.196 StartY=279.742 StartZ=0 EndX=180.166 EndY=269.772 EndZ=0
    g13: LineSegment StartX=180.166 StartY=269.772 StartZ=0 EndX=190.136 EndY=279.742 EndZ=0
    g14: LineSegment StartX=190.136 StartY=279.742 StartZ=0 EndX=180.166 EndY=289.713 EndZ=0
    g15: GeomPoint X=180.166 Y=279.742 Z=0
    g16: LineSegment StartX=162.488 StartY=262.065 StartZ=0 EndX=180.166 EndY=279.742 EndZ=0
    g17: LineSegment StartX=179.194 StartY=255.33 StartZ=0 EndX=180.166 EndY=269.772 EndZ=0
    g18: LineSegment StartX=170.196 StartY=279.742 StartZ=0 EndX=155.753 EndY=278.77 EndZ=0
  constraints (49):
    c: Coincident(g0,g1)
    c: Coincident(g1,g2)
    c: Coincident(g2,g3)
    c: Coincident(g3,g0)
    c: Symmetric(g2,g0,g4)
    c: Equal(g0,g1)
    c: Parallel(g1,g3)
    c: Parallel(g2,g0)
    c: Perpendicular(g1,g0)
    c: Distance(g1) = 14.1
    c: Coincident(g5,g6)
    c: Coincident(g6,g7)
    c: Coincident(g7,g8)
    c: Coincident(g8,g5)
    c: Symmetric(g7,g5,g9)
    c: Equal(g5,g6)
    c: Parallel(g5,g7)
    c: Parallel(g6,g8)
    c: Perpendicular(g5,g6)
    c: Parallel(g6,g1)
    c: Coincident(g10,g4)
    c: Coincident(g10,g9)
    c: Perpendicular(g2,g10)
    c: Equal(g1,g6)
    c: Distance(g10) = 19.05
    c: Coincident(g11,g12)
    c: Coincident(g12,g13)
    c: Coincident(g13,g14)
    c: Coincident(g14,g11)
    c: Symmetric(g13,g11,g15)
    c: Parallel(g13,g11)
    c: Parallel(g12,g14)
    c: Perpendicular(g12,g11)
    c: Equal(g12,g3)
    c: Equal(g12,g11)
    c: PointOnObject(g16,g10)
    c: Coincident(g16,g15)
    c: Perpendicular(g10,g16)
    c: Perpendicular(g12,g16)
    c: Angle(g10,g-1) = 0.785398
    c: Coincident(g17,g7)
    c: Coincident(g17,g12)
    c: Coincident(g18,g11)
    c: Coincident(g18,g0)
    c: Equal(g18,g17)
    c: DistanceX(g7,g-3) = 22
    c: DistanceY(g7,g-3) = 9.97038
    c: Block(g10)
    c: Distance(g16) = 25
FEATURE [PartDesign::Pocket] Pocket020
  BaseFeature = -> BaseFeature002
  Direction = (0,0,-1)
  Length = 5
  Length2 = 5
  Profile = -> Sketch029
  ReferenceAxis = -> Sketch029 [N_Axis]
  Type = 1
FEATURE [Sketcher::SketchObject] Sketch030
  AttachmentOffset = pos=(0,0,1.5) rot=(0,0,1;0rad)
  ExternalGeometry = -> [Pocket020]
  FullyConstrained = true
  MapMode = 5
  Placement = pos=(0,0,1.5) rot=(0,0,1;0rad)
  Support = -> [XY_Plane013]
  expr: .AttachmentOffset.Base.z = Spreadsheet.h_plate
  sketch-geometry (20):
    g0: LineSegment StartX=101.875 StartY=160 StartZ=0 EndX=101.875 EndY=268.536 EndZ=0
    g1: LineSegment StartX=101.875 StartY=268.536 StartZ=0 EndX=180.166 EndY=295.713 EndZ=0
    g2: LineSegment StartX=180.166 StartY=295.713 StartZ=0 EndX=335.212 EndY=273.3 EndZ=0
    g3: LineSegment StartX=335.212 StartY=273.3 StartZ=0 EndX=335.212 EndY=160 EndZ=0
    g4: LineSegment StartX=335.212 StartY=160 StartZ=0 EndX=101.875 EndY=160 EndZ=0
    g5: LineSegment StartX=116.675 StartY=222.5 StartZ=0 EndX=116.675 EndY=166 EndZ=0
    g6: LineSegment StartX=116.675 StartY=166 StartZ=0 EndX=113.875 EndY=166 EndZ=0
    g7: LineSegment StartX=113.875 StartY=166 StartZ=0 EndX=113.875 EndY=222.5 EndZ=0
    g8: LineSegment StartX=113.875 StartY=222.5 StartZ=0 EndX=116.675 EndY=222.5 EndZ=0
    g9: GeomPoint X=115.275 Y=194.25 Z=0
    g10: LineSegment StartX=139.525 StartY=222.5 StartZ=0 EndX=139.525 EndY=166 EndZ=0
    g11: LineSegment StartX=139.525 StartY=166 StartZ=0 EndX=136.725 EndY=166 EndZ=0
    g12: LineSegment StartX=136.725 StartY=166 StartZ=0 EndX=136.725 EndY=222.5 EndZ=0
    g13: LineSegment StartX=136.725 StartY=222.5 StartZ=0 EndX=139.525 EndY=222.5 EndZ=0
    g14: GeomPoint X=138.125 Y=194.25 Z=0
    g15: LineSegment StartX=155.753 StartY=278.77 StartZ=0 EndX=153.13 EndY=286.328 EndZ=0
    g16: LineSegment StartX=0 StartY=0 StartZ=0 EndX=600 EndY=0 EndZ=0
    g17: LineSegment StartX=600 StartY=0 StartZ=0 EndX=600 EndY=600 EndZ=0
    g18: LineSegment StartX=600 StartY=600 StartZ=0 EndX=0 EndY=600 EndZ=0
    g19: LineSegment StartX=0 StartY=600 StartZ=0 EndX=0 EndY=0 EndZ=0
  constraints (59):
    c: Coincident(g0,g1)
    c: Coincident(g1,g2)
    c: Coincident(g2,g3)
    c: Vertical(g3)
    c: Coincident(g3,g4)
    c: Coincident(g4,g0)
    c: Horizontal(g4)
    c: Coincident(g5,g6)
    c: Coincident(g6,g7)
    c: Coincident(g7,g8)
    c: Coincident(g8,g5)
    c: Vertical(g5)
    c: Vertical(g7)
    c: Horizontal(g6)
    c: Horizontal(g8)
    c: Symmetric(g7,g5,g9)
    c: Coincident(g10,g11)
    c: Coincident(g11,g12)
    c: Coincident(g12,g13)
    c: Coincident(g13,g10)
    c: Vertical(g10)
    c: Vertical(g12)
    c: Horizontal(g11)
    c: Horizontal(g13)
    c: Symmetric(g12,g10,g14)
    c: DistanceX(g9,g14) = 22.85
    c: PointOnObject(g7,g13)
    c: Equal(g7,g10)
    c: Equal(g6,g11)
    c: DistanceX(g8,g8) = 2.8
    c: DistanceY(g7,g7) = 56.5
    c: DistanceY(g3,g-3) = 15
    c: DistanceX(g-3,g3) = 8
    c: DistanceY(g0,g6) = 6
    c: DistanceX(g0,g6) = 12
    c: DistanceY(g-5,g1) = 6
    c: DistanceX(g1,g-5) = 0
    c: Coincident(g15,g-6)
    c: PointOnObject(g15,g1)
    c: Perpendicular(g1,g15)
    c: Distance(g15) = 8
    c: Coincident(g16,g17)
    c: Coincident(g17,g18)
    c: Coincident(g18,g19)
    c: Coincident(g19,g16)
    c: Horizontal(g16)
    c: Horizontal(g18)
    c: Vertical(g17)
    c: Vertical(g19)
    c: Distance(g17,g19) = 600
    c: Distance(g16,g18) = 600
    c: Coincident(g16,g-1)
    c: Block(g3)
    c: Block(g2)
    c: Block(g1)
    c: Block(g12)
    c: Vertical(g0)
    c: DistanceY(g-7,g2) = 8
    c: DistanceX(g10,g-4) = 45
FEATURE [PartDesign::Pocket] Pocket021
  BaseFeature = -> Pocket020
  Direction = (0,0,-1)
  Length = 5
  Length2 = 5
  Profile = -> Sketch030
  ReferenceAxis = -> Sketch030 [N_Axis]
  Type = 1
FEATURE [Sketcher::SketchObject] Sketch031
  AttachmentOffset = pos=(0,0,1.5) rot=(0,0,1;0rad)
  ExternalGeometry = -> [Sketch030]
  FullyConstrained = true
  MapMode = 5
  Placement = pos=(0,0,1.5) rot=(0,0,1;0rad)
  Support = -> [XY_Plane013]
  expr: .AttachmentOffset.Base.z = Spreadsheet.h_plate
  expr: Constraints[39] = Spreadsheet.d_wall_out
  sketch-geometry (16):
    g0: LineSegment StartX=101.875 StartY=160 StartZ=0 EndX=101.875 EndY=268.536 EndZ=0
    g1: LineSegment StartX=101.875 StartY=268.536 StartZ=0 EndX=180.166 EndY=295.713 EndZ=0
    g2: LineSegment StartX=180.166 StartY=295.713 StartZ=0 EndX=335.212 EndY=273.3 EndZ=0
    g3: LineSegment StartX=335.212 StartY=273.3 StartZ=0 EndX=335.212 EndY=160 EndZ=0
    g4: LineSegment StartX=335.212 StartY=160 StartZ=0 EndX=101.875 EndY=160 EndZ=0
    g5: LineSegment StartX=103.875 StartY=162 StartZ=0 EndX=103.875 EndY=267.23 EndZ=0
    g6: LineSegment StartX=103.875 StartY=267.23 StartZ=0 EndX=180.166 EndY=293.713 EndZ=0
    g7: LineSegment StartX=180.166 StartY=293.713 StartZ=0 EndX=333.212 EndY=271.589 EndZ=0
    g8: LineSegment StartX=333.212 StartY=271.589 StartZ=0 EndX=333.212 EndY=162 EndZ=0
    g9: LineSegment StartX=333.212 StartY=162 StartZ=0 EndX=103.875 EndY=162 EndZ=0
    g10: LineSegment StartX=103.875 StartY=162 StartZ=0 EndX=103.875 EndY=160 EndZ=0
    g11: LineSegment StartX=103.875 StartY=162 StartZ=0 EndX=101.875 EndY=162 EndZ=0
    g12: LineSegment StartX=103.875 StartY=267.23 StartZ=0 EndX=101.875 EndY=267.23 EndZ=0
    g13: LineSegment StartX=180.166 StartY=295.713 StartZ=0 EndX=180.166 EndY=293.713 EndZ=0
    g14: LineSegment StartX=333.212 StartY=271.589 StartZ=0 EndX=335.212 EndY=271.589 EndZ=0
    g15: LineSegment StartX=333.212 StartY=162 StartZ=0 EndX=335.212 EndY=162 EndZ=0
  constraints (42):
    c: Coincident(g-4,g0)
    c: Coincident(g0,g-7)
    c: Coincident(g0,g1)
    c: Coincident(g1,g-7)
    c: Coincident(g1,g2)
    c: Coincident(g2,g-6)
    c: Coincident(g2,g3)
    c: Coincident(g3,g-5)
    c: Coincident(g3,g4)
    c: Coincident(g4,g0)
    c: Coincident(g5,g6)
    c: Coincident(g5,g9)
    c: Coincident(g6,g7)
    c: Coincident(g7,g8)
    c: Coincident(g8,g9)
    c: Coincident(g10,g5)
    c: PointOnObject(g10,g4)
    c: Vertical(g10)
    c: Coincident(g11,g5)
    c: PointOnObject(g11,g0)
    c: Horizontal(g11)
    c: Equal(g11,g10)
    c: Coincident(g12,g5)
    c: PointOnObject(g12,g0)
    c: Coincident(g13,g1)
    c: Coincident(g6,g13)
    c: Vertical(g13)
    c: Horizontal(g12)
    c: Coincident(g14,g7)
    c: PointOnObject(g14,g3)
    c: Horizontal(g14)
    c: Parallel(g7,g2)
    c: Coincident(g15,g8)
    c: PointOnObject(g15,g3)
    c: Horizontal(g15)
    c: Equal(g15,g14)
    c: Equal(g14,g13)
    c: Equal(g13,g12)
    c: Equal(g12,g11)
    c: DistanceX(g11,g11) = 2
    c: Horizontal(g9)
    c: Parallel(g6,g1)
FEATURE [PartDesign::Pad] Pad029
  BaseFeature = -> Pocket021
  Direction = (0,0,1)
  Length = 15
  Length2 = 10
  Profile = -> Sketch031
  ReferenceAxis = -> Sketch031 [N_Axis]
  Type = 0
  expr: Length = Spreadsheet.h_wall_out
FEATURE [Sketcher::SketchObject] Sketch032
  AttachmentOffset = pos=(0,0,1.5) rot=(0,0,1;0rad)
  FullyConstrained = true
  MapMode = 5
  Placement = pos=(0,0,1.5) rot=(0,0,1;0rad)
  Support = -> [XY_Plane013]
  expr: .AttachmentOffset.Base.z = Spreadsheet.h_plate
  sketch-geometry (6):
    g0: LineSegment StartX=194.05 StartY=191.575 StartZ=0 EndX=333.212 EndY=191.575 EndZ=0
    g1: LineSegment StartX=333.212 StartY=190.8 StartZ=0 EndX=333.212 EndY=192.35 EndZ=0
    g2: LineSegment StartX=333.212 StartY=192.35 StartZ=0 EndX=178.212 EndY=192.35 EndZ=0
    g3: LineSegment StartX=178.212 StartY=192.35 StartZ=0 EndX=178.212 EndY=190.8 EndZ=0
    g4: LineSegment StartX=178.212 StartY=190.8 StartZ=0 EndX=333.212 EndY=190.8 EndZ=0
    g5: GeomPoint X=255.712 Y=191.575 Z=0
  constraints (14):
    c: Coincident(g1,g2)
    c: Coincident(g2,g3)
    c: Coincident(g3,g4)
    c: Coincident(g4,g1)
    c: Vertical(g1)
    c: Vertical(g3)
    c: Horizontal(g2)
    c: Horizontal(g4)
    c: Symmetric(g3,g1,g5)
    c: PointOnObject(g5,g0)
    c: Block(g0)
    c: DistanceY(g3,g3) = 1.55
    c: PointOnObject(g0,g1)
    c: DistanceX(g4,g4) = 155
FEATURE [PartDesign::Pad] Pad030
  BaseFeature = -> Pad029
  Direction = (0,0,1)
  Length = 10
  Length2 = 10
  Profile = -> Sketch032
  ReferenceAxis = -> Sketch032 [N_Axis]
  Type = 3
  UpToFace = -> Pad029 [Face161]
FEATURE [PartDesign::LinearPattern] LinearPattern001
  BaseFeature = -> Pad030
  Direction = -> Y_Axis013
  Length = 57.15
  Mode = 1
  Occurrences = 4
  Offset = 19.05
  Originals = -> [Pad030]
  expr: Offset = Spreadsheet.d_key
FEATURE [PartDesign::Pad] Pad031
  BaseFeature = -> LinearPattern001
  Direction = (-1,0,0)
  Length = 2
  Length2 = 10
  Profile = -> LinearPattern001 [Face167]
  Type = 0
  expr: Length = Spreadsheet.d_wall_out
FEATURE [PartDesign::Pad] Pad032
  BaseFeature = -> Pad031
  Direction = (0,-1,0)
  Length = 10
  Length2 = 10
  Profile = -> Pad031 [Face169]
  Type = 2
FEATURE [Sketcher::SketchObject] Sketch033
  AttachmentOffset = pos=(0,0,1.5) rot=(0,0,1;0rad)
  ExternalGeometry = -> [Pad032]
  FullyConstrained = true
  MapMode = 5
  Placement = pos=(0,0,1.5) rot=(0,0,1;0rad)
  Support = -> [XY_Plane013]
  expr: .AttachmentOffset.Base.z = Spreadsheet.h_plate
  expr: Constraints[11] = Spreadsheet.d_wall_out
  expr: Constraints[25] = Spreadsheet.d_wall_out
  sketch-geometry (10):
    g0: LineSegment StartX=178.212 StartY=230.45 StartZ=0 EndX=103.875 EndY=267.23 EndZ=0
    g1: LineSegment StartX=103.875 StartY=267.23 StartZ=0 EndX=103.875 EndY=264.999 EndZ=0
    g2: LineSegment StartX=103.875 StartY=264.999 StartZ=0 EndX=178.212 EndY=228.219 EndZ=0
    g3: LineSegment StartX=178.212 StartY=228.219 StartZ=0 EndX=178.212 EndY=230.45 EndZ=0
    g4: LineSegment StartX=178.212 StartY=230.45 StartZ=0 EndX=177.326 EndY=228.657 EndZ=0
    g5: LineSegment StartX=176.212 StartY=249.5 StartZ=0 EndX=215.014 EndY=288.675 EndZ=0
    g6: LineSegment StartX=215.014 StartY=288.675 StartZ=0 EndX=217.8 EndY=288.273 EndZ=0
    g7: LineSegment StartX=217.8 StartY=288.273 StartZ=0 EndX=179.027 EndY=249.5 EndZ=0
    g8: LineSegment StartX=179.027 StartY=249.5 StartZ=0 EndX=176.212 EndY=249.5 EndZ=0
    g9: LineSegment StartX=179.027 StartY=249.5 StartZ=0 EndX=177.606 EndY=250.907 EndZ=0
  constraints (27):
    c: Coincident(g-3,g0)
    c: Coincident(g0,g-4)
    c: Coincident(g0,g1)
    c: Vertical(g1)
    c: Coincident(g1,g2)
    c: Coincident(g2,g3)
    c: Coincident(g3,g0)
    c: Vertical(g3)
    c: Coincident(g4,g0)
    c: PointOnObject(g4,g2)
    c: Perpendicular(g2,g4)
    c: Distance(g4) = 2
    c: Equal(g1,g3)
    c: Coincident(g-5,g5)
    c: PointOnObject(g5,g-6)
    c: Coincident(g5,g6)
    c: PointOnObject(g6,g-6)
    c: Coincident(g6,g7)
    c: PointOnObject(g7,g-5)
    c: Coincident(g7,g8)
    c: Coincident(g8,g5)
    c: Equal(g8,g6)
    c: Coincident(g9,g7)
    c: PointOnObject(g9,g5)
    c: Perpendicular(g5,g9)
    c: Distance(g9) = 2
    c: Angle(g-1,g7) = 0.785398
FEATURE [PartDesign::Pad] Pad033
  BaseFeature = -> Pad032
  Direction = (0,0,1)
  Length = 8
  Length2 = 10
  Profile = -> Sketch033
  ReferenceAxis = -> Sketch033 [N_Axis]
  Type = 0
  expr: Length = Spreadsheet.h_wall_in
FEATURE [PartDesign::Pocket] Pocket022
  BaseFeature = -> Pad033
  Direction = (0,0,-1)
  Length = 0
  Length2 = 5
  Profile = -> Pad033 [Face201]
  Type = 3
  UpToFace = -> Pad033 [Face202]
FEATURE [PartDesign::Pocket] Pocket023
  BaseFeature = -> Pocket022
  Direction = (0,0,1)
  Length = 0.2
  Length2 = 5
  Profile = -> Pocket022 [Face1]
  Type = 0
FEATURE [Sketcher::SketchObject] Sketch034
  ExternalGeometry = -> [Pocket023]
  FullyConstrained = false
  MapMode = 5
  Placement = pos=(0,0,0.2) rot=(1,0,0;3.14159rad)
  Support = -> [Pocket023]
  sketch-geometry (8):
    g0: LineSegment StartX=222.758 StartY=-249.5 StartZ=0 EndX=222.758 EndY=-268.032 EndZ=0
    g1: LineSegment StartX=222.758 StartY=-268.032 StartZ=0 EndX=240.883 EndY=-268.032 EndZ=0
    g2: LineSegment StartX=240.883 StartY=-268.032 StartZ=0 EndX=240.883 EndY=-249.5 EndZ=0
    g3: LineSegment StartX=240.883 StartY=-249.5 StartZ=0 EndX=222.758 EndY=-249.5 EndZ=0
    g4: LineSegment StartX=73.3224 StartY=-133.323 StartZ=0 EndX=73.3224 EndY=-375.955 EndZ=0
    g5: LineSegment StartX=73.3224 StartY=-375.955 StartZ=0 EndX=516.325 EndY=-375.955 EndZ=0
    g6: LineSegment StartX=516.325 StartY=-375.955 StartZ=0 EndX=516.325 EndY=-133.323 EndZ=0
    g7: LineSegment StartX=516.325 StartY=-133.323 StartZ=0 EndX=73.3224 EndY=-133.323 EndZ=0
  constraints (17):
    c: Coincident(g0,g1)
    c: Coincident(g1,g2)
    c: Coincident(g2,g3)
    c: Coincident(g3,g0)
    c: Vertical(g0)
    c: Vertical(g2)
    c: Horizontal(g1)
    c: Horizontal(g3)
    c: PointOnObject(g0,g-4)
    c: Coincident(g4,g5)
    c: Coincident(g5,g6)
    c: Coincident(g6,g7)
    c: Coincident(g7,g4)
    c: Vertical(g4)
    c: Vertical(g6)
    c: Horizontal(g5)
    c: Horizontal(g7)
FEATURE [PartDesign::Pocket] Pocket024
  BaseFeature = -> Pocket023
  Direction = (0,0,1)
  Length = 5
  Length2 = 5
  Profile = -> Sketch034
  ReferenceAxis = -> Sketch034 [N_Axis]
  Type = 1
FEATURE [PartDesign::Body] Body003  label="plate_right_v2"
  BaseFeature = -> baseplate_right_v004_solid001
  Group = -> [BaseFeature002,Sketch029,Pocket020,Sketch030,Pocket021,Sketch031,Pad029,Sketch032,Pad030,LinearPattern001,Pad031,Pad032,Sketch033,Pad033,Pocket022,Pocket023,Sketch034,Pocket024]
  Origin = -> Origin013
  Tip = -> Pocket023
PROVENANCE & LICENSES
A FreeCAD (.FCStd) document from a public repository crawl; recipes are the document's own serialized feature recipes (and, for linked parts, companion documents' recipes).
License: as declared in the source repository (recorded in the dataset sidecar).
